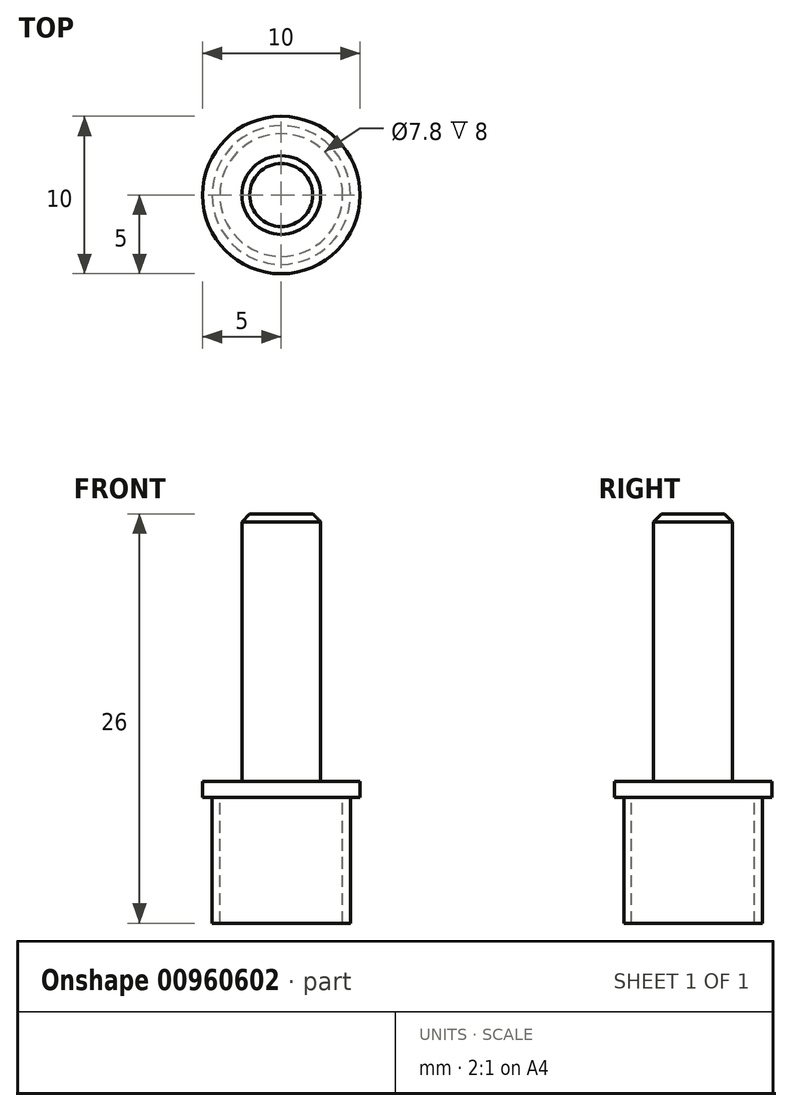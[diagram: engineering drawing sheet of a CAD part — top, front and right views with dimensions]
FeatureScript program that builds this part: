
annotation { "Feature Type Name" : "Feature", "Feature Type Description" : "" }
export const myFeature = defineFeature(function(context is Context, id is Id, definition is map)
    precondition{}
    {
        {
            var Q0;
            Q0=qCreatedBy(makeId("Front.planeOp"),FACE);
            var sketch = newSketch(context, id + "F0", { "sketchPlane" : qUnion([Q0])});
            skLineSegment(sketch, "E0", {"start": v(0, 28.64) * mm, "end": v(0, 10.64) * mm});
            skLineSegment(sketch, "E1", {"start": v(0, 10.64) * mm, "end": v(-3.9, 10.64) * mm});
            skLineSegment(sketch, "E2", {"start": v(-3.9, 10.64) * mm, "end": v(-3.9, 2.64) * mm});
            skLineSegment(sketch, "E3", {"start": v(-3.9, 2.64) * mm, "end": v(-4.4, 2.64) * mm});
            skLineSegment(sketch, "E4", {"start": v(-4.4, 2.64) * mm, "end": v(-4.4, 10.64) * mm});
            skLineSegment(sketch, "E5", {"start": v(-4.4, 10.64) * mm, "end": v(-5, 10.64) * mm});
            skLineSegment(sketch, "E6", {"start": v(-5, 10.64) * mm, "end": v(-5, 11.64) * mm});
            skLineSegment(sketch, "E7", {"start": v(-5, 11.64) * mm, "end": v(-2.5, 11.64) * mm});
            skLineSegment(sketch, "E8", {"start": v(-2.5, 11.64) * mm, "end": v(-2.5, 28.64) * mm});
            skLineSegment(sketch, "E9", {"start": v(0, 28.64) * mm, "end": v(-2.5, 28.64) * mm});
            skSolve(sketch);
        }
        {
            var Q0;
            Q0=makeQuery(id+"F0.imprint","IMPRINT",FACE,{"disambiguationData":[TD([[makeQuery(id+"F0.imprint","IMPRINT",EDGE,{"derivedFrom":sQuery(id+"F0.wireOp",EDGE,"E0")}),-1.0]])]});
            var Q1;
            Q1=sQuery(id+"F0.wireOp",EDGE,"E0");
            revolve(context, id + "F1", {"surfaceOperationType" : NewSurfaceOperationType.NEW, "entities" : qUnion([Q0]), "axis" : qUnion([Q1]), "revolveType" : RevolveType.FULL});
        }
        {
            var Q0;
            Q0=makeQuery(id+"F1.opRevolve","SWEPT_EDGE",EDGE,{"disambiguationData":[OSD([sQuery(id+"F0.wireOp",EDGE,"E8"),sQuery(id+"F0.wireOp",EDGE,"E9")])]});
            chamfer(context, id + "F2", {"entities" : qUnion([Q0]), "width" : 0.5 * mm, "tangentPropagation" : true});
        }
    });
